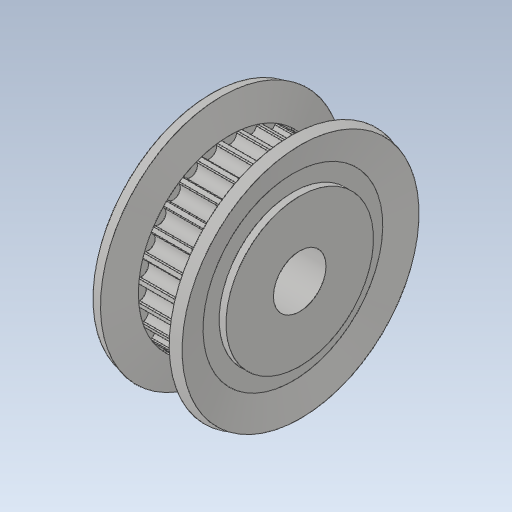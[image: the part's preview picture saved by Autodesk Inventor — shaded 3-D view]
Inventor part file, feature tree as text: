
AUTODESK INVENTOR PART (.ipt)
format: ipt  version: 2024 (Build 280153000, 153)  size: 346,112 bytes
history: native  units: mm
features: sketch x5, revolve x3, extrude x1, pattern_circular x1, hole x1
ambient origin geometry x8: Origin, YZ Plane, XZ Plane, XY Plane, X Axis, Y Axis, Z Axis, Center Point
bodies: Solid1 (feature_tree)
feature tree (11):
  revolve  "Revolution1"  [1 undecoded]
  extrude  "Extrusion1"  TaperAngle=360.0deg  [1 undecoded]
  pattern_circular  "Circular Pattern1"  [2 undecoded]
  revolve  "Revolution2"  [1 undecoded]
  revolve  "Revolution3"  [1 undecoded]
  hole  "Hole1"  [1 undecoded]
  sketch  "Sketch_16"  dims[d3=280.0mm d4=2.243995mm d6=360.0deg]
  sketch  "Sketch_18"  dims[d7=360.0deg]
  sketch  "Sketch_20"  dims[d8=5.0mm d9=6.0mm d10=4.0mm d11=2.0mm d12=90.0deg d13=8.3mm d14=0.0mm]
  sketch  "Sketch_21"
  sketch  "Sketch5"  dims[d0=360.0deg d1=5.0mm d2=0.0mm]
note: 7 required parameter values undecoded (feature->parameter linkage not recoverable at this tier; creation-order binding heuristic only, values carry confidence <= 0.55)